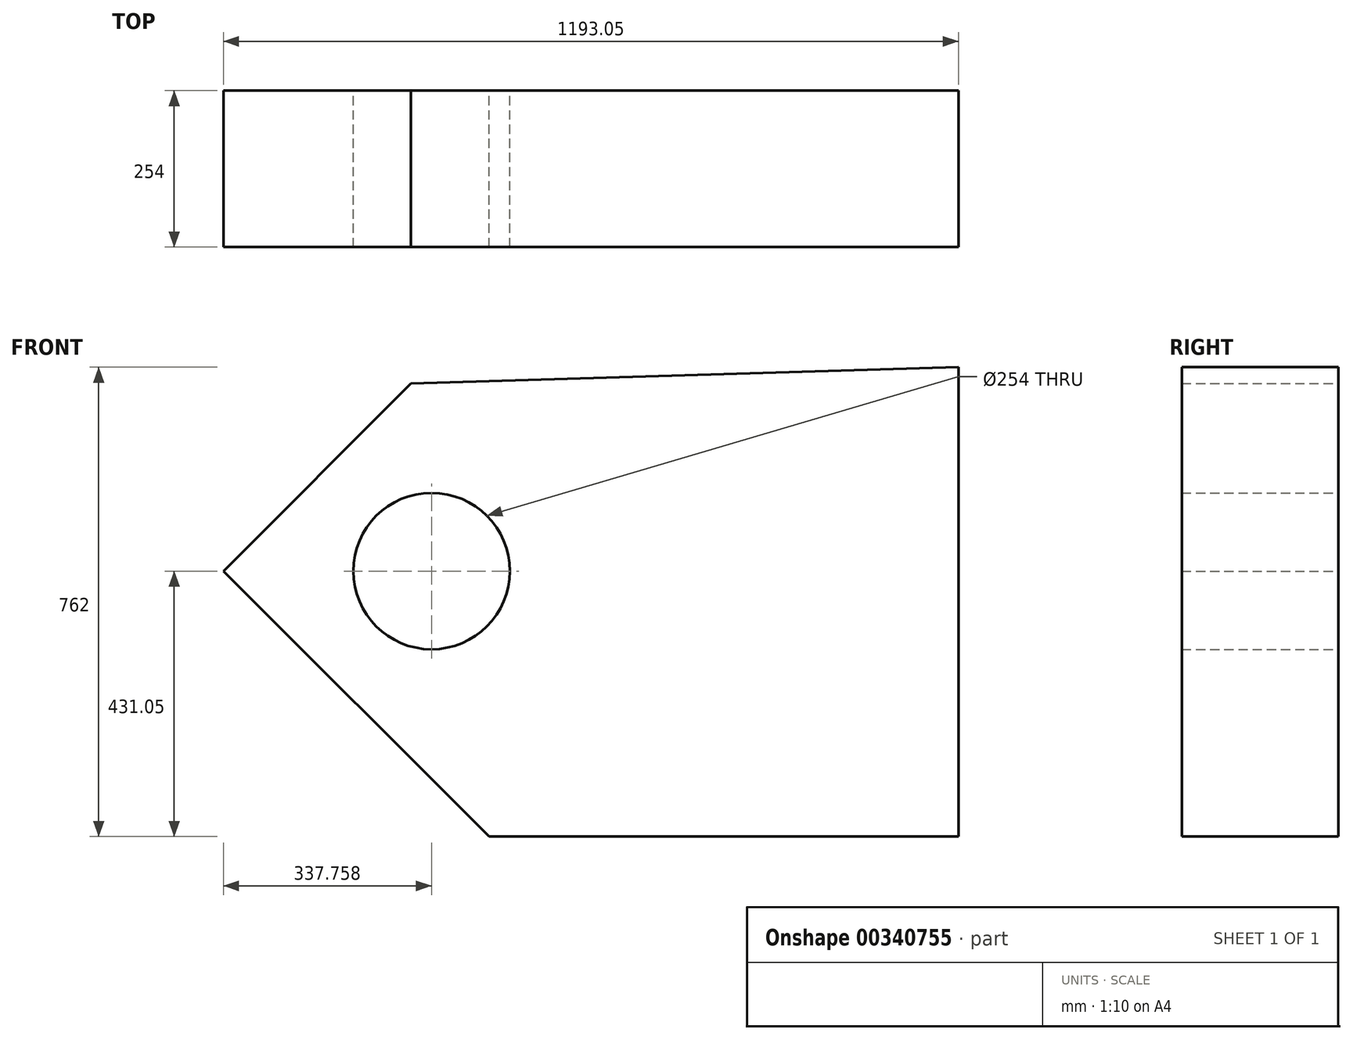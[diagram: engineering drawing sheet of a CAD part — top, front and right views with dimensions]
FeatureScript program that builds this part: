
annotation { "Feature Type Name" : "Feature", "Feature Type Description" : "" }
export const myFeature = defineFeature(function(context is Context, id is Id, definition is map)
    precondition{}
    {
        {
            var Q0;
            Q0=qCreatedBy(makeId("Front.planeOp"),FACE);
            var sketch = newSketch(context, id + "F0", { "sketchPlane" : qUnion([Q0])});
            skLineSegment(sketch, "E0", {"start": v(-341.6, 304.45) * mm, "end": v(-646.05, 0) * mm});
            skLineSegment(sketch, "E1", {"start": v(-646.05, 0) * mm, "end": v(-215, -431.05) * mm});
            skLineSegment(sketch, "E2", {"start": v(-215, -431.05) * mm, "end": v(547, -431.05) * mm});
            skLineSegment(sketch, "E3", {"start": v(547, -431.05) * mm, "end": v(547, 330.95) * mm});
            skLineSegment(sketch, "E4", {"start": v(547, 330.95) * mm, "end": v(-341.6, 304.45) * mm});
            skCircle(sketch, "E5", {"center": v(-308.3, 0) * mm, "radius": 127 * mm});
            skSolve(sketch);
        }
        {
            var Q0;
            Q0=makeQuery(id+"F0.imprint","IMPRINT",FACE,{"disambiguationData":[TD([[makeQuery(id+"F0.imprint","IMPRINT",EDGE,{"derivedFrom":sQuery(id+"F0.wireOp",EDGE,"E0")}),1.0]])]});
            extrude(context, id + "F1", {"entities" : qUnion([Q0]), "depth" : 254 * mm});
        }
    });
